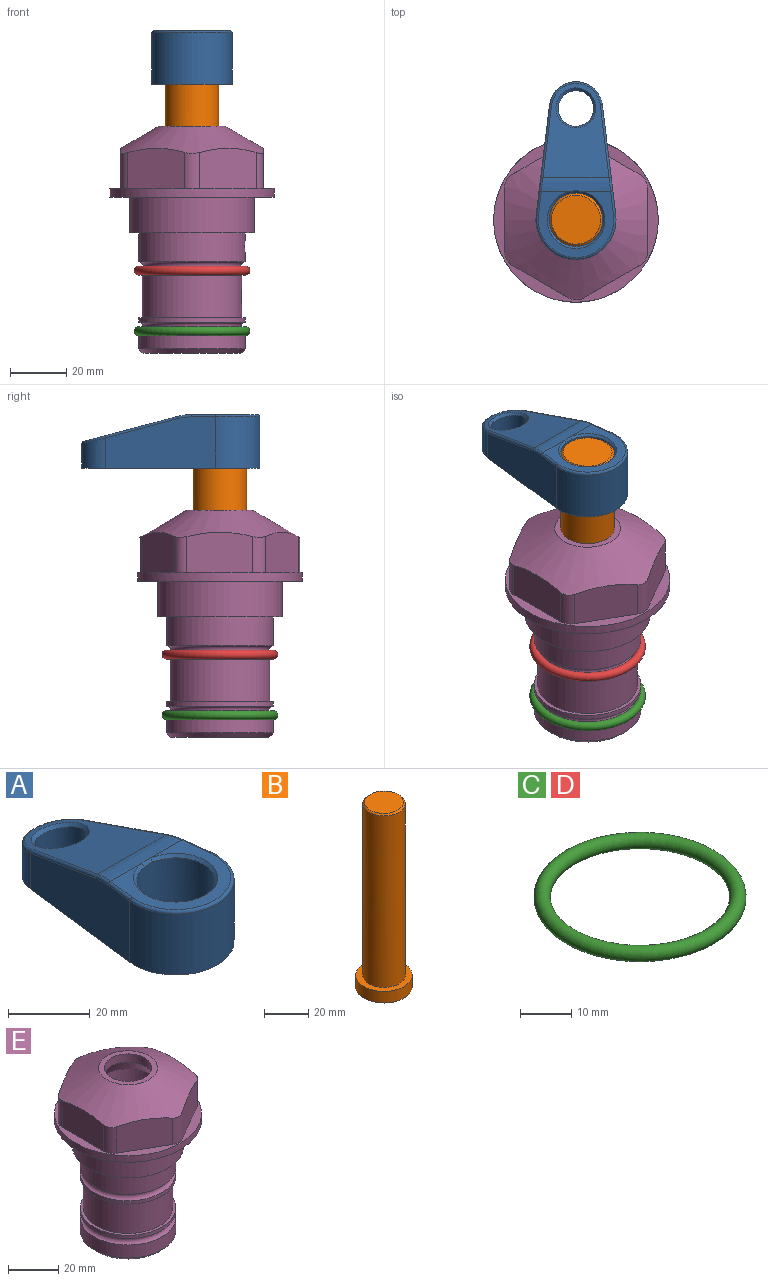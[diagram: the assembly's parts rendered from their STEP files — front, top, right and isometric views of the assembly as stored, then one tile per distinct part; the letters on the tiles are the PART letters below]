
ASSEMBLY  parts=5 mates=4
PART A: 31 faces, bbox 31.7x65.5x19.8 mm
  f0: plane 39.12x18.26mm, normal (0.99,0.12,0), area 612.2mm2, adj f1,f4,f7,f11,f13,f15
  f1: cylinder r=9.53mm len=18.91mm, axis (0,0,-1), area 296.1mm2, adj f0,f2,f7,f17
  f2: plane 39.12x18.26mm, normal (-0.99,0.12,0), area 612.2mm2, adj f1,f4,f7,f12,f14,f16
  f3: cylinder r=6.35mm len=12.7mm, axis (0,0,-1), area 362.4mm2, adj f7,f18
  f4: cylinder r=14.29mm len=28.58mm, axis (0,0,-1), area 882.2mm2, adj f0,f2,f7,f10
  f5: cylinder r=9.53mm len=19.05mm, axis (0,0,-1), area 1092.6mm2, adj f7,f19,f20
  f6: plane 26.99x23.69mm, normal (0,0,1), area 216.2mm2, adj f9,f10,f11,f12,f19
  f7: plane 63.5x28.58mm, normal (0,0,-1), area 661.8mm2, adj f0,f1,f2,f3,f4,f5,f22,f23
  f8: plane 33.52x23.6mm, normal (0,0.26,0.97), area 486mm2, adj f9,f15,f16,f17,f18
  f9: cylinder r=19.05mm len=24.72mm, axis (1,0,0), area 120.4mm2, adj f6,f8,f13,f14,f20
  f10: torus R=13.49mm, axis (0,0,1), area 59mm2, adj f4,f6,f11,f12
  f11: cylinder r=0.79mm len=8.67mm, axis (0.12,-0.99,0), area 10.8mm2, adj f0,f6,f10,f13
  f12: cylinder r=0.79mm len=8.67mm, axis (0.12,0.99,0), area 10.8mm2, adj f2,f6,f10,f14
  f13: bspline ~4.95x1.42mm, area 6.1mm2, adj f0,f9,f11,f15
  f14: bspline ~4.95x1.42mm, area 6.1mm2, adj f2,f9,f12,f16
  f15: cylinder r=0.79mm len=25.95mm, axis (0.12,-0.96,0.26), area 32.9mm2, adj f0,f8,f13,f17
  f16: cylinder r=0.79mm len=25.95mm, axis (0.12,0.96,-0.26), area 32.9mm2, adj f2,f8,f14,f17
  f17: bspline ~18.91x8.38mm, area 30mm2, adj f1,f8,f15,f16
  f18: bspline ~14.29x14.29mm, area 48.3mm2, adj f3,f8
  f19: cone r=9.53mm half-angle=45deg, axis (0,0,1), area 66.5mm2, adj f5,f6,f20
  f20: bspline ~3.22x0.96mm, area 3.5mm2, adj f5,f9,f19
  f21: plane 2.75x2.72mm, normal (0,0,-1), area 2.9mm2, adj f23,f25,f28
  f22: plane 23.05x15.88mm, normal (-0.99,-0.12,0), area 323.6mm2, adj f7,f25,f26,f27,f28,f29
  f23: plane 23.05x15.88mm, normal (0.99,-0.12,0), area 323.6mm2, adj f7,f21,f25,f27,f28,f30
  f24: cylinder r=9.53mm len=10.69mm, axis (0,0,-1), area 114.7mm2, adj f7,f27,f29,f30
  f25: cylinder r=12.7mm len=20.59mm, axis (0,0,-1), area 381.1mm2, adj f7,f21,f22,f23,f26,f28
  f26: plane 2.75x2.72mm, normal (0,0,-1), area 2.9mm2, adj f22,f25,f28
  f27: plane 19.72x18.37mm, normal (0,-0.26,-0.97), area 291.8mm2, adj f22,f23,f24,f28,f29,f30
  f28: cylinder r=15.88mm len=19.92mm, axis (1,0,0), area 54.8mm2, adj f21,f22,f23,f25,f26,f27
  f29: cylinder r=1.59mm len=11mm, axis (0,0,-1), area 34.7mm2, adj f7,f22,f24,f27
  f30: cylinder r=1.59mm len=11mm, axis (0,0,-1), area 34.7mm2, adj f7,f23,f24,f27
PART B: 6 faces, bbox 25.4x25.4x101.6 mm
  f0: plane 17.46x17.46mm, normal (0,0,1), area 239.5mm2, adj f5
  f1: plane 25.4x25.4mm, normal (0,0,-1), area 506.7mm2, adj f2
  f2: cylinder r=12.7mm len=25.4mm, axis (0,0,1), area 506.7mm2, adj f1,f3
  f3: plane 25.4x25.4mm, normal (0,0,1), area 221.7mm2, adj f2,f4
  f4: cylinder r=9.53mm len=94.46mm, axis (0,0,1), area 5653mm2, adj f3,f5
  f5: cone r=8.73mm half-angle=45deg, axis (0,0,-1), area 64.4mm2, adj f0,f4
PART C: 1 faces, bbox 44.7x44.7x3.2 mm
  f0: torus R=19.05mm, axis (0,0,1), area 1193.9mm2
PART D: same geometry as C
PART E: 36 faces, bbox 58.7x58.7x81 mm
  f0: cylinder r=17.78mm len=35.56mm, axis (0,0,1), area 1670.8mm2, adj f23,f24,f31
  f1: cylinder r=19.05mm len=38.1mm, axis (0,0,1), area 1191.9mm2, adj f26,f27,f30
  f2: plane 58.66x58.66mm, normal (0,0,-1), area 1150.6mm2, adj f3,f28
  f3: cylinder r=29.33mm len=58.66mm, axis (0,0,-1), area 585.1mm2, adj f2,f4
  f4: plane 58.66x58.66mm, normal (0,0,1), area 475.9mm2, adj f3,f5,f6,f7,f8,f9,f10,f11
  f5: plane 20.32x14.34mm, normal (-0.5,0.87,0), area 324.4mm2, adj f4,f15,f16,f17
  f6: plane 20.32x14.34mm, normal (0.5,0.87,0), area 324.4mm2, adj f4,f14,f15,f17
  f7: plane 23.48x14.34mm, normal (1,0,0), area 324.4mm2, adj f4,f13,f14,f17
  f8: plane 20.32x14.34mm, normal (0.5,-0.87,0), area 324.4mm2, adj f4,f12,f13,f17
  f9: plane 20.32x14.34mm, normal (-0.5,-0.87,0), area 324.4mm2, adj f4,f11,f12,f17
  f10: plane 23.48x14.34mm, normal (-1,0,0), area 324.4mm2, adj f4,f11,f16,f17
  f11: cylinder r=5.08mm len=12.85mm, axis (0,0,-1), area 67.2mm2, adj f4,f9,f10,f17
  f12: cylinder r=5.08mm len=12.85mm, axis (0,0,-1), area 67.2mm2, adj f4,f8,f9,f17
  f13: cylinder r=5.08mm len=12.85mm, axis (0,0,-1), area 67.2mm2, adj f4,f7,f8,f17
  f14: cylinder r=5.08mm len=12.85mm, axis (0,0,-1), area 67.2mm2, adj f4,f6,f7,f17
  f15: cylinder r=5.08mm len=12.85mm, axis (0,0,-1), area 67.2mm2, adj f4,f5,f6,f17
  f16: cylinder r=5.08mm len=12.85mm, axis (0,0,-1), area 67.2mm2, adj f4,f5,f10,f17
  f17: cone r=11.73mm half-angle=60deg, axis (0,0,-1), area 2071.8mm2, adj f5,f6,f7,f8,f9,f10,f11,f12
  f18: plane 23.46x23.46mm, normal (0,0,1), area 147.4mm2, adj f17,f35
  f19: plane 34.93x34.93mm, normal (0,0,-1), area 958mm2, adj f29
  f20: cylinder r=19.05mm len=38.1mm, axis (0,0,1), area 760.1mm2, adj f21,f29
  f21: torus R=19.05mm, axis (0,0,1), area 565.3mm2, adj f20,f22
  f22: cylinder r=19.05mm len=38.1mm, axis (0,0,1), area 190mm2, adj f21,f23
  f23: plane 38.1x38.1mm, normal (0,0,1), area 146.9mm2, adj f0,f22
  f24: plane 38.1x38.1mm, normal (0,0,-1), area 146.9mm2, adj f0,f25
  f25: cylinder r=19.05mm len=38.1mm, axis (0,0,1), area 190mm2, adj f24,f26
  f26: torus R=19.05mm, axis (0,0,1), area 565.3mm2, adj f1,f25
  f27: plane 44.45x44.45mm, normal (0,0,-1), area 411.7mm2, adj f1,f28
  f28: cylinder r=22.23mm len=44.45mm, axis (0,0,1), area 1773.5mm2, adj f2,f27
  f29: cone r=19.05mm half-angle=45deg, axis (0,0,1), area 257.5mm2, adj f19,f20
  f30: cylinder r=3.17mm len=6.75mm, axis (-1,0,0), area 128mm2, adj f1,f33
  f31: cylinder r=3.17mm len=6.35mm, axis (-1,0,0), area 102.5mm2, adj f0,f33
  f32: plane 25.4x25.4mm, normal (0,0,1), area 506.7mm2, adj f33
  f33: cylinder r=12.7mm len=66.42mm, axis (0,0,-1), area 5236.2mm2, adj f30,f31,f32,f34
  f34: cone r=9.53mm half-angle=30deg, axis (0,0,-1), area 443.4mm2, adj f33,f35
  f35: cylinder r=9.53mm len=19.05mm, axis (0,0,-1), area 240.9mm2, adj f18,f34
PLACE A t=(0,0,8.67)mm
PLACE B t=(0,0,7.87)mm
PLACE C t=(0,0,-10.48)mm
PLACE D t=(0,0,11.11)mm
PLACE E t=(0,0,12.7)mm
MATE fastened D.f0 <-> E.f0  axis (0,0,1) through (0,0,-13.4)mm
MATE fastened C.f0 <-> E.f0  axis (0,0,1) through (0,0,-34.99)mm
MATE cylindrical B.f2 <-> E.f0  axis (0,0,-1) through (0,0,-30.23)mm
MATE fastened B.f2 <-> A.f4  axis (0,0,1) through (0,0,71.37)mm
